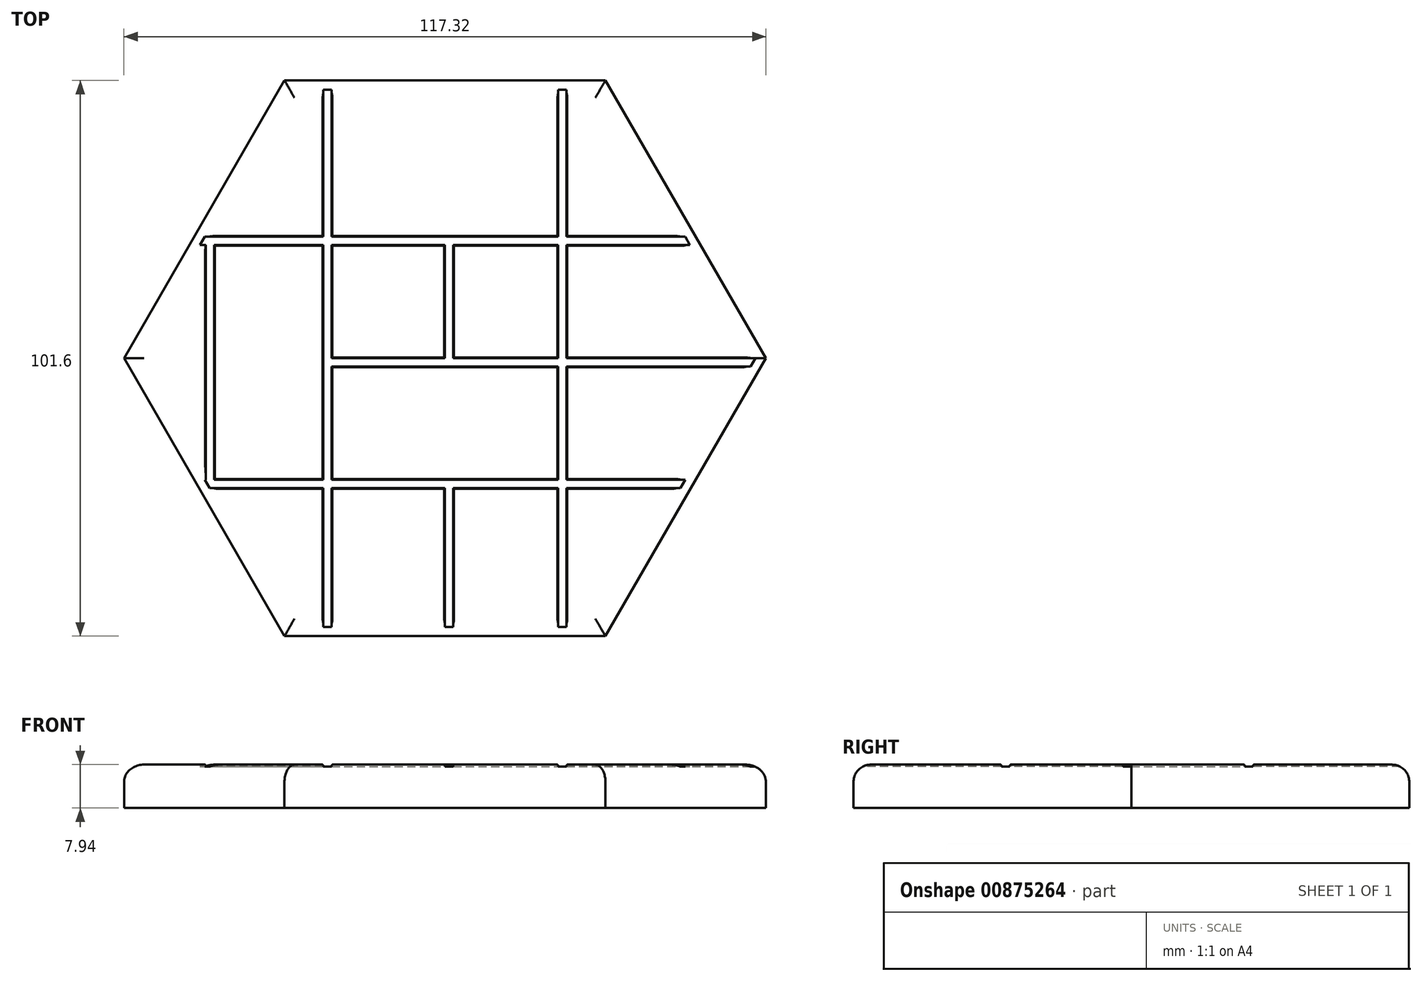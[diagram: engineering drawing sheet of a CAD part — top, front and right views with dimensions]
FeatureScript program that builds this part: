
annotation { "Feature Type Name" : "Feature", "Feature Type Description" : "" }
export const myFeature = defineFeature(function(context is Context, id is Id, definition is map)
    precondition{}
    {
        {
            var Q0;
            Q0=qCreatedBy(makeId("Top.planeOp"),FACE);
            var sketch = newSketch(context, id + "F0", { "sketchPlane" : qUnion([Q0])});
            skCircle(sketch, "E0.cCircle", {"center": v(0, 0) * mm, "radius": 50.8 * mm, "construction": true});
            skLineSegment(sketch, "E0.0", {"start": v(58.66, 0) * mm, "end": v(29.33, -50.8) * mm});
            skLineSegment(sketch, "E0.1", {"start": v(29.33, -50.8) * mm, "end": v(-29.33, -50.8) * mm});
            skLineSegment(sketch, "E0.2", {"start": v(-29.33, -50.8) * mm, "end": v(-58.66, 0) * mm});
            skLineSegment(sketch, "E0.3", {"start": v(-58.66, 0) * mm, "end": v(-29.33, 50.8) * mm});
            skLineSegment(sketch, "E0.4", {"start": v(-29.33, 50.8) * mm, "end": v(29.33, 50.8) * mm});
            skLineSegment(sketch, "E0.5", {"start": v(29.33, 50.8) * mm, "end": v(58.66, 0) * mm});
            skPoint(sketch, "E0.0.midPoint", {"position": v(44, -25.4) * mm});
            skSolve(sketch);
        }
        {
            var Q0;
            Q0 = qSketchRegion(id + "F0", true);
            extrude(context, id + "F1", {"entities" : qUnion([Q0]), "depth" : 7.94 * mm, "offsetDistance" : 25.4 * mm});
        }
        {
            var Q0;
            Q0=makeQuery(id+"F1.opExtrude","CAP_EDGE",EDGE,{"disambiguationData":[OSD([sQuery(id+"F0.wireOp",EDGE,"E0.2")])],"isStart":false});
            var Q1;
            Q1=makeQuery(id+"F1.opExtrude","CAP_EDGE",EDGE,{"disambiguationData":[OSD([sQuery(id+"F0.wireOp",EDGE,"E0.1")])],"isStart":false});
            var Q2;
            Q2=makeQuery(id+"F1.opExtrude","CAP_EDGE",EDGE,{"disambiguationData":[OSD([sQuery(id+"F0.wireOp",EDGE,"E0.0")])],"isStart":false});
            var Q3;
            Q3=makeQuery(id+"F1.opExtrude","CAP_EDGE",EDGE,{"disambiguationData":[OSD([sQuery(id+"F0.wireOp",EDGE,"E0.5")])],"isStart":false});
            var Q4;
            Q4=makeQuery(id+"F1.opExtrude","CAP_EDGE",EDGE,{"disambiguationData":[OSD([sQuery(id+"F0.wireOp",EDGE,"E0.4")])],"isStart":false});
            var Q5;
            Q5=makeQuery(id+"F1.opExtrude","CAP_EDGE",EDGE,{"disambiguationData":[OSD([sQuery(id+"F0.wireOp",EDGE,"E0.3")])],"isStart":false});
            fillet(context, id + "F2", {"entities" : qUnion([Q0, Q1, Q2, Q3, Q4, Q5]), "radius" : 3.17 * mm, "tangentPropagation" : true, "allowEdgeOverflow" : false});
        }
        {
            var Q0;
            Q0=makeQuery(id+"F1.opExtrude","CAP_FACE",FACE,{"disambiguationData":[OSD([sQuery(id+"F0.wireOp",EDGE,"E0.0"),sQuery(id+"F0.wireOp",EDGE,"E0.1"),sQuery(id+"F0.wireOp",EDGE,"E0.2"),sQuery(id+"F0.wireOp",EDGE,"E0.3"),sQuery(id+"F0.wireOp",EDGE,"E0.4"),sQuery(id+"F0.wireOp",EDGE,"E0.5")])],"isStart":false});
            var sketch = newSketch(context, id + "F3", { "sketchPlane" : qUnion([Q0])});
            skLineSegment(sketch, "E1", {"start": v(-22.23, 58.85) * mm, "end": v(-22.22, -59.57) * mm});
            skLineSegment(sketch, "E2", {"start": v(22.22, 59.72) * mm, "end": v(22.23, -61.08) * mm});
            skLineSegment(sketch, "E3", {"start": v(-65.38, 22.23) * mm, "end": v(65.6, 22.23) * mm});
            skLineSegment(sketch, "E4", {"start": v(-66.46, -22.23) * mm, "end": v(67.33, -22.23) * mm});
            skLineSegment(sketch, "E5", {"start": v(-22.23, 0) * mm, "end": v(71.88, 0) * mm});
            skPoint(sketch, "E5.startSnap0", {"position": v(-22.23, -0.36) * mm});
            skLineSegment(sketch, "E6", {"start": v(-42.16, -22.23) * mm, "end": v(-42.16, 22.23) * mm});
            skLineSegment(sketch, "E7", {"start": v(0, -57.56) * mm, "end": v(0, -22.23) * mm});
            skLineSegment(sketch, "E8", {"start": v(0, 0) * mm, "end": v(0, 22.23) * mm});
            skLineSegment(sketch, "E9.0", {"start": v(-20.7, 58.85) * mm, "end": v(-20.7, -59.57) * mm});
            skLineSegment(sketch, "E10.0", {"start": v(20.7, 59.72) * mm, "end": v(20.7, -61.08) * mm});
            skLineSegment(sketch, "E11.0", {"start": v(-65.38, 20.7) * mm, "end": v(65.6, 20.7) * mm});
            skLineSegment(sketch, "E12.0", {"start": v(1.52, 0) * mm, "end": v(1.52, 22.23) * mm});
            skLineSegment(sketch, "E13.0", {"start": v(-66.46, -23.75) * mm, "end": v(67.33, -23.75) * mm});
            skLineSegment(sketch, "E14.0", {"start": v(-22.23, -1.52) * mm, "end": v(71.88, -1.52) * mm});
            skLineSegment(sketch, "E15.0", {"start": v(-43.69, -22.23) * mm, "end": v(-43.69, 22.23) * mm});
            skLineSegment(sketch, "E16.0", {"start": v(1.52, -57.64) * mm, "end": v(1.52, -22.23) * mm});
            skLineSegment(sketch, "E17", {"start": v(-65.38, 22.23) * mm, "end": v(-65.38, 20.7) * mm});
            skLineSegment(sketch, "E18", {"start": v(-66.46, -22.23) * mm, "end": v(-66.46, -23.75) * mm});
            skLineSegment(sketch, "E19", {"start": v(-22.23, 58.85) * mm, "end": v(-20.7, 58.85) * mm});
            skLineSegment(sketch, "E20", {"start": v(22.22, 59.72) * mm, "end": v(20.7, 59.72) * mm});
            skLineSegment(sketch, "E21", {"start": v(65.6, 20.7) * mm, "end": v(65.6, 22.23) * mm});
            skLineSegment(sketch, "E22", {"start": v(71.88, 0) * mm, "end": v(71.88, -1.52) * mm});
            skLineSegment(sketch, "E23", {"start": v(67.33, -22.23) * mm, "end": v(67.33, -23.75) * mm});
            skLineSegment(sketch, "E24", {"start": v(22.23, -61.08) * mm, "end": v(20.7, -61.08) * mm});
            skLineSegment(sketch, "E25", {"start": v(1.52, -57.64) * mm, "end": v(0, -57.56) * mm});
            skLineSegment(sketch, "E26", {"start": v(-20.7, -59.57) * mm, "end": v(-22.22, -59.57) * mm});
            skSolve(sketch);
        }
        {
            var Q0;
            {var subQ0=sQuery(id+"F3.wireOp",EDGE,"E19");Q0=makeQuery(id+"F3.imprint","IMPRINT",FACE,{"disambiguationData":[TD([[makeQuery(id+"F3.imprint","IMPRINT",EDGE,{"derivedFrom":subQ0}),-1.0]])]});}
            var Q1;
            {var subQ0=sQuery(id+"F3.wireOp",EDGE,"E3");var subQ1=sQuery(id+"F3.wireOp",EDGE,"E1");var subQ2=makeQuery(id+"F3.imprint","INTERSECT",VERTEX,{"derivedFrom":[subQ1,subQ0]});Q1=makeQuery(id+"F3.imprint","IMPRINT",FACE,{"disambiguationData":[TD([[makeQuery(id+"F3.imprint","IMPRINT",EDGE,{"disambiguationData":[TD([[subQ2,-1.0]])],"derivedFrom":subQ0}),1.0]])]});}
            var Q2;
            {var subQ0=sQuery(id+"F3.wireOp",EDGE,"E3");var subQ1=sQuery(id+"F3.wireOp",EDGE,"E2");var subQ2=makeQuery(id+"F3.imprint","INTERSECT",VERTEX,{"derivedFrom":[subQ1,subQ0]});Q2=makeQuery(id+"F3.imprint","IMPRINT",FACE,{"disambiguationData":[TD([[makeQuery(id+"F3.imprint","IMPRINT",EDGE,{"disambiguationData":[TD([[subQ2,1.0]])],"derivedFrom":subQ0}),1.0]])]});}
            var Q3;
            {var subQ0=sQuery(id+"F3.wireOp",EDGE,"E20");Q3=makeQuery(id+"F3.imprint","IMPRINT",FACE,{"disambiguationData":[TD([[makeQuery(id+"F3.imprint","IMPRINT",EDGE,{"derivedFrom":subQ0}),1.0]])]});}
            var Q4;
            {var subQ0=sQuery(id+"F3.wireOp",EDGE,"E3");var subQ1=sQuery(id+"F3.wireOp",EDGE,"E2");var subQ2=makeQuery(id+"F3.imprint","INTERSECT",VERTEX,{"derivedFrom":[subQ1,subQ0]});Q4=makeQuery(id+"F3.imprint","IMPRINT",FACE,{"disambiguationData":[TD([[makeQuery(id+"F3.imprint","IMPRINT",EDGE,{"disambiguationData":[TD([[subQ2,-1.0]])],"derivedFrom":subQ1}),1.0]])]});}
            var Q5;
            {var subQ0=sQuery(id+"F3.wireOp",EDGE,"E21");Q5=makeQuery(id+"F3.imprint","IMPRINT",FACE,{"disambiguationData":[TD([[makeQuery(id+"F3.imprint","IMPRINT",EDGE,{"derivedFrom":subQ0}),1.0]])]});}
            var Q6;
            {var subQ0=sQuery(id+"F3.wireOp",EDGE,"E3");var subQ1=sQuery(id+"F3.wireOp",EDGE,"E2");var subQ2=makeQuery(id+"F3.imprint","INTERSECT",VERTEX,{"derivedFrom":[subQ1,subQ0]});Q6=makeQuery(id+"F3.imprint","IMPRINT",FACE,{"disambiguationData":[TD([[makeQuery(id+"F3.imprint","IMPRINT",EDGE,{"disambiguationData":[TD([[subQ2,-1.0]])],"derivedFrom":subQ1}),-1.0]])]});}
            var Q7;
            {var subQ0=sQuery(id+"F3.wireOp",EDGE,"E11.0");var subQ1=sQuery(id+"F3.wireOp",EDGE,"E2");var subQ2=makeQuery(id+"F3.imprint","INTERSECT",VERTEX,{"derivedFrom":[subQ1,subQ0]});Q7=makeQuery(id+"F3.imprint","IMPRINT",FACE,{"disambiguationData":[TD([[makeQuery(id+"F3.imprint","IMPRINT",EDGE,{"disambiguationData":[TD([[subQ2,-1.0]])],"derivedFrom":subQ1}),-1.0]])]});}
            var Q8;
            {var subQ0=sQuery(id+"F3.wireOp",EDGE,"E12.0");var subQ1=sQuery(id+"F3.wireOp",EDGE,"E3");var subQ2=makeQuery(id+"F3.imprint","INTERSECT",VERTEX,{"derivedFrom":[subQ1,subQ0]});Q8=makeQuery(id+"F3.imprint","IMPRINT",FACE,{"disambiguationData":[TD([[makeQuery(id+"F3.imprint","IMPRINT",EDGE,{"disambiguationData":[TD([[subQ2,-1.0]])],"derivedFrom":subQ1}),-1.0]])]});}
            var Q9;
            {var subQ0=sQuery(id+"F3.wireOp",EDGE,"E5");var subQ1=sQuery(id+"F3.wireOp",EDGE,"E2");var subQ2=makeQuery(id+"F3.imprint","INTERSECT",VERTEX,{"derivedFrom":[subQ1,subQ0]});Q9=makeQuery(id+"F3.imprint","IMPRINT",FACE,{"disambiguationData":[TD([[makeQuery(id+"F3.imprint","IMPRINT",EDGE,{"disambiguationData":[TD([[subQ2,-1.0]])],"derivedFrom":subQ1}),1.0]])]});}
            var Q10;
            {var subQ0=sQuery(id+"F3.wireOp",EDGE,"E5");var subQ1=sQuery(id+"F3.wireOp",EDGE,"E2");var subQ2=makeQuery(id+"F3.imprint","INTERSECT",VERTEX,{"derivedFrom":[subQ1,subQ0]});Q10=makeQuery(id+"F3.imprint","IMPRINT",FACE,{"disambiguationData":[TD([[makeQuery(id+"F3.imprint","IMPRINT",EDGE,{"disambiguationData":[TD([[subQ2,-1.0]])],"derivedFrom":subQ1}),-1.0]])]});}
            var Q11;
            {var subQ1=sQuery(id+"F3.wireOp",EDGE,"E5");var subQ8=makeQuery(id+"F3.imprint","INTERSECT",VERTEX,{"derivedFrom":[subQ1,sQuery(id+"F3.wireOp",EDGE,"E8")]});Q11=makeQuery(id+"F3.imprint","IMPRINT",FACE,{"disambiguationData":[TD([[makeQuery(id+"F3.imprint","IMPRINT",EDGE,{"disambiguationData":[TD([[subQ8,1.0]])],"derivedFrom":subQ1}),-1.0]])]});}
            var Q12;
            {var subQ0=sQuery(id+"F3.wireOp",EDGE,"E14.0");var subQ1=sQuery(id+"F3.wireOp",EDGE,"E2");var subQ2=makeQuery(id+"F3.imprint","INTERSECT",VERTEX,{"derivedFrom":[subQ1,subQ0]});Q12=makeQuery(id+"F3.imprint","IMPRINT",FACE,{"disambiguationData":[TD([[makeQuery(id+"F3.imprint","IMPRINT",EDGE,{"disambiguationData":[TD([[subQ2,-1.0]])],"derivedFrom":subQ1}),-1.0]])]});}
            var Q13;
            {var subQ0=sQuery(id+"F3.wireOp",EDGE,"E8");var subQ1=sQuery(id+"F3.wireOp",EDGE,"E5");var subQ2=makeQuery(id+"F3.imprint","INTERSECT",VERTEX,{"derivedFrom":[subQ1,subQ0]});Q13=makeQuery(id+"F3.imprint","IMPRINT",FACE,{"disambiguationData":[TD([[makeQuery(id+"F3.imprint","IMPRINT",EDGE,{"disambiguationData":[TD([[subQ2,-1.0]])],"derivedFrom":subQ1}),1.0]])]});}
            var Q14;
            {var subQ0=sQuery(id+"F3.wireOp",EDGE,"E8");var subQ1=sQuery(id+"F3.wireOp",EDGE,"E3");var subQ2=makeQuery(id+"F3.imprint","INTERSECT",VERTEX,{"derivedFrom":[subQ1,subQ0]});Q14=makeQuery(id+"F3.imprint","IMPRINT",FACE,{"disambiguationData":[TD([[makeQuery(id+"F3.imprint","IMPRINT",EDGE,{"disambiguationData":[TD([[subQ2,-1.0]])],"derivedFrom":subQ1}),-1.0]])]});}
            var Q15;
            {var subQ0=sQuery(id+"F3.wireOp",EDGE,"E8");var subQ1=sQuery(id+"F3.wireOp",EDGE,"E3");var subQ2=makeQuery(id+"F3.imprint","INTERSECT",VERTEX,{"derivedFrom":[subQ1,subQ0]});Q15=makeQuery(id+"F3.imprint","IMPRINT",FACE,{"disambiguationData":[TD([[makeQuery(id+"F3.imprint","IMPRINT",EDGE,{"disambiguationData":[TD([[subQ2,1.0]])],"derivedFrom":subQ1}),-1.0]])]});}
            var Q16;
            {var subQ0=sQuery(id+"F3.wireOp",EDGE,"E3");var subQ1=sQuery(id+"F3.wireOp",EDGE,"E1");var subQ2=makeQuery(id+"F3.imprint","INTERSECT",VERTEX,{"derivedFrom":[subQ1,subQ0]});Q16=makeQuery(id+"F3.imprint","IMPRINT",FACE,{"disambiguationData":[TD([[makeQuery(id+"F3.imprint","IMPRINT",EDGE,{"disambiguationData":[TD([[subQ2,-1.0]])],"derivedFrom":subQ1}),1.0]])]});}
            var Q17;
            {var subQ0=sQuery(id+"F3.wireOp",EDGE,"E5");var subQ1=sQuery(id+"F3.wireOp",EDGE,"E1");var subQ2=makeQuery(id+"F3.imprint","INTERSECT",VERTEX,{"derivedFrom":[subQ1,subQ0]});Q17=makeQuery(id+"F3.imprint","IMPRINT",FACE,{"disambiguationData":[TD([[makeQuery(id+"F3.imprint","IMPRINT",EDGE,{"disambiguationData":[TD([[subQ2,1.0]])],"derivedFrom":subQ1}),1.0]])]});}
            var Q18;
            {var subQ0=sQuery(id+"F3.wireOp",EDGE,"E3");var subQ1=sQuery(id+"F3.wireOp",EDGE,"E1");var subQ2=makeQuery(id+"F3.imprint","INTERSECT",VERTEX,{"derivedFrom":[subQ1,subQ0]});Q18=makeQuery(id+"F3.imprint","IMPRINT",FACE,{"disambiguationData":[TD([[makeQuery(id+"F3.imprint","IMPRINT",EDGE,{"disambiguationData":[TD([[subQ2,-1.0]])],"derivedFrom":subQ1}),-1.0]])]});}
            var Q19;
            {var subQ8=sQuery(id+"F3.wireOp",EDGE,"E11.0");var subQ9=sQuery(id+"F3.wireOp",EDGE,"E6");var subQ10=makeQuery(id+"F3.imprint","INTERSECT",VERTEX,{"derivedFrom":[subQ9,subQ8]});Q19=makeQuery(id+"F3.imprint","IMPRINT",FACE,{"disambiguationData":[TD([[makeQuery(id+"F3.imprint","IMPRINT",EDGE,{"disambiguationData":[TD([[subQ10,1.0]])],"derivedFrom":subQ8}),-1.0]])]});}
            var Q20;
            {var subQ0=sQuery(id+"F3.wireOp",EDGE,"E17");Q20=makeQuery(id+"F3.imprint","IMPRINT",FACE,{"disambiguationData":[TD([[makeQuery(id+"F3.imprint","IMPRINT",EDGE,{"derivedFrom":subQ0}),1.0]])]});}
            var Q21;
            {var subQ0=sQuery(id+"F3.wireOp",EDGE,"E6");var subQ4=sQuery(id+"F3.wireOp",EDGE,"E11.0");var subQ5=makeQuery(id+"F3.imprint","INTERSECT",VERTEX,{"derivedFrom":[subQ0,subQ4]});Q21=makeQuery(id+"F3.imprint","IMPRINT",FACE,{"disambiguationData":[TD([[makeQuery(id+"F3.imprint","IMPRINT",EDGE,{"disambiguationData":[TD([[subQ5,1.0]])],"derivedFrom":subQ4}),1.0]])]});}
            var Q22;
            {var subQ0=sQuery(id+"F3.wireOp",EDGE,"E3");var subQ4=sQuery(id+"F3.wireOp",EDGE,"E15.0");var subQ5=makeQuery(id+"F3.imprint","INTERSECT",VERTEX,{"derivedFrom":[subQ0,subQ4]});Q22=makeQuery(id+"F3.imprint","IMPRINT",FACE,{"disambiguationData":[TD([[makeQuery(id+"F3.imprint","IMPRINT",EDGE,{"disambiguationData":[TD([[subQ5,1.0]])],"derivedFrom":subQ4}),-1.0]])]});}
            var Q23;
            {var subQ0=sQuery(id+"F3.wireOp",EDGE,"E15.0");var subQ1=sQuery(id+"F3.wireOp",EDGE,"E11.0");var subQ2=makeQuery(id+"F3.imprint","INTERSECT",VERTEX,{"derivedFrom":[subQ1,subQ0]});Q23=makeQuery(id+"F3.imprint","IMPRINT",FACE,{"disambiguationData":[TD([[makeQuery(id+"F3.imprint","IMPRINT",EDGE,{"disambiguationData":[TD([[subQ2,-1.0]])],"derivedFrom":subQ1}),-1.0]])]});}
            var Q24;
            {var subQ0=sQuery(id+"F3.wireOp",EDGE,"E18");Q24=makeQuery(id+"F3.imprint","IMPRINT",FACE,{"disambiguationData":[TD([[makeQuery(id+"F3.imprint","IMPRINT",EDGE,{"derivedFrom":subQ0}),1.0]])]});}
            var Q25;
            {var subQ0=sQuery(id+"F3.wireOp",EDGE,"E4");var subQ4=sQuery(id+"F3.wireOp",EDGE,"E15.0");var subQ5=makeQuery(id+"F3.imprint","INTERSECT",VERTEX,{"derivedFrom":[subQ0,subQ4]});Q25=makeQuery(id+"F3.imprint","IMPRINT",FACE,{"disambiguationData":[TD([[makeQuery(id+"F3.imprint","IMPRINT",EDGE,{"disambiguationData":[TD([[subQ5,-1.0]])],"derivedFrom":subQ4}),-1.0]])]});}
            var Q26;
            {var subQ0=sQuery(id+"F3.wireOp",EDGE,"E4");var subQ1=sQuery(id+"F3.wireOp",EDGE,"E1");var subQ2=makeQuery(id+"F3.imprint","INTERSECT",VERTEX,{"derivedFrom":[subQ1,subQ0]});Q26=makeQuery(id+"F3.imprint","IMPRINT",FACE,{"disambiguationData":[TD([[makeQuery(id+"F3.imprint","IMPRINT",EDGE,{"disambiguationData":[TD([[subQ2,-1.0]])],"derivedFrom":subQ1}),1.0]])]});}
            var Q27;
            {var subQ0=sQuery(id+"F3.wireOp",EDGE,"E14.0");var subQ1=sQuery(id+"F3.wireOp",EDGE,"E1");var subQ2=makeQuery(id+"F3.imprint","INTERSECT",VERTEX,{"derivedFrom":[subQ1,subQ0]});Q27=makeQuery(id+"F3.imprint","IMPRINT",FACE,{"disambiguationData":[TD([[makeQuery(id+"F3.imprint","IMPRINT",EDGE,{"disambiguationData":[TD([[subQ2,-1.0]])],"derivedFrom":subQ1}),1.0]])]});}
            var Q28;
            {var subQ0=sQuery(id+"F3.wireOp",EDGE,"E5");var subQ1=sQuery(id+"F3.wireOp",EDGE,"E1");var subQ2=makeQuery(id+"F3.imprint","INTERSECT",VERTEX,{"derivedFrom":[subQ1,subQ0]});Q28=makeQuery(id+"F3.imprint","IMPRINT",FACE,{"disambiguationData":[TD([[makeQuery(id+"F3.imprint","IMPRINT",EDGE,{"disambiguationData":[TD([[subQ2,-1.0]])],"derivedFrom":subQ1}),1.0]])]});}
            var Q29;
            {var subQ0=sQuery(id+"F3.wireOp",EDGE,"E13.0");var subQ1=sQuery(id+"F3.wireOp",EDGE,"E1");var subQ2=makeQuery(id+"F3.imprint","INTERSECT",VERTEX,{"derivedFrom":[subQ1,subQ0]});Q29=makeQuery(id+"F3.imprint","IMPRINT",FACE,{"disambiguationData":[TD([[makeQuery(id+"F3.imprint","IMPRINT",EDGE,{"disambiguationData":[TD([[subQ2,-1.0]])],"derivedFrom":subQ0}),-1.0]])]});}
            var Q30;
            {var subQ0=sQuery(id+"F3.wireOp",EDGE,"E7");var subQ1=sQuery(id+"F3.wireOp",EDGE,"E4");var subQ2=makeQuery(id+"F3.imprint","INTERSECT",VERTEX,{"derivedFrom":[subQ1,subQ0]});Q30=makeQuery(id+"F3.imprint","IMPRINT",FACE,{"disambiguationData":[TD([[makeQuery(id+"F3.imprint","IMPRINT",EDGE,{"disambiguationData":[TD([[subQ2,1.0]])],"derivedFrom":subQ1}),-1.0]])]});}
            var Q31;
            {var subQ0=sQuery(id+"F3.wireOp",EDGE,"E7");var subQ1=sQuery(id+"F3.wireOp",EDGE,"E4");var subQ2=makeQuery(id+"F3.imprint","INTERSECT",VERTEX,{"derivedFrom":[subQ1,subQ0]});Q31=makeQuery(id+"F3.imprint","IMPRINT",FACE,{"disambiguationData":[TD([[makeQuery(id+"F3.imprint","IMPRINT",EDGE,{"disambiguationData":[TD([[subQ2,-1.0]])],"derivedFrom":subQ1}),-1.0]])]});}
            var Q32;
            {var subQ0=sQuery(id+"F3.wireOp",EDGE,"E16.0");var subQ1=sQuery(id+"F3.wireOp",EDGE,"E4");var subQ2=makeQuery(id+"F3.imprint","INTERSECT",VERTEX,{"derivedFrom":[subQ1,subQ0]});Q32=makeQuery(id+"F3.imprint","IMPRINT",FACE,{"disambiguationData":[TD([[makeQuery(id+"F3.imprint","IMPRINT",EDGE,{"disambiguationData":[TD([[subQ2,-1.0]])],"derivedFrom":subQ1}),-1.0]])]});}
            var Q33;
            {var subQ0=sQuery(id+"F3.wireOp",EDGE,"E13.0");var subQ1=sQuery(id+"F3.wireOp",EDGE,"E7");var subQ2=makeQuery(id+"F3.imprint","INTERSECT",VERTEX,{"derivedFrom":[subQ1,subQ0]});Q33=makeQuery(id+"F3.imprint","IMPRINT",FACE,{"disambiguationData":[TD([[makeQuery(id+"F3.imprint","IMPRINT",EDGE,{"disambiguationData":[TD([[subQ2,-1.0]])],"derivedFrom":subQ0}),-1.0]])]});}
            var Q34;
            {var subQ6=sQuery(id+"F3.wireOp",EDGE,"E22");Q34=makeQuery(id+"F3.imprint","IMPRINT",FACE,{"disambiguationData":[TD([[makeQuery(id+"F3.imprint","IMPRINT",EDGE,{"derivedFrom":subQ6}),-1.0]])]});}
            var Q35;
            {var subQ0=sQuery(id+"F3.wireOp",EDGE,"E23");Q35=makeQuery(id+"F3.imprint","IMPRINT",FACE,{"disambiguationData":[TD([[makeQuery(id+"F3.imprint","IMPRINT",EDGE,{"derivedFrom":subQ0}),-1.0]])]});}
            var Q36;
            {var subQ0=sQuery(id+"F3.wireOp",EDGE,"E4");var subQ1=sQuery(id+"F3.wireOp",EDGE,"E2");var subQ2=makeQuery(id+"F3.imprint","INTERSECT",VERTEX,{"derivedFrom":[subQ1,subQ0]});Q36=makeQuery(id+"F3.imprint","IMPRINT",FACE,{"disambiguationData":[TD([[makeQuery(id+"F3.imprint","IMPRINT",EDGE,{"disambiguationData":[TD([[subQ2,-1.0]])],"derivedFrom":subQ1}),1.0]])]});}
            var Q37;
            {var subQ0=sQuery(id+"F3.wireOp",EDGE,"E4");var subQ1=sQuery(id+"F3.wireOp",EDGE,"E2");var subQ2=makeQuery(id+"F3.imprint","INTERSECT",VERTEX,{"derivedFrom":[subQ1,subQ0]});Q37=makeQuery(id+"F3.imprint","IMPRINT",FACE,{"disambiguationData":[TD([[makeQuery(id+"F3.imprint","IMPRINT",EDGE,{"disambiguationData":[TD([[subQ2,-1.0]])],"derivedFrom":subQ1}),-1.0]])]});}
            var Q38;
            {var subQ0=sQuery(id+"F3.wireOp",EDGE,"E24");Q38=makeQuery(id+"F3.imprint","IMPRINT",FACE,{"disambiguationData":[TD([[makeQuery(id+"F3.imprint","IMPRINT",EDGE,{"derivedFrom":subQ0}),-1.0]])]});}
            var Q39;
            {var subQ0=sQuery(id+"F3.wireOp",EDGE,"E13.0");var subQ1=sQuery(id+"F3.wireOp",EDGE,"E2");var subQ2=makeQuery(id+"F3.imprint","INTERSECT",VERTEX,{"derivedFrom":[subQ1,subQ0]});Q39=makeQuery(id+"F3.imprint","IMPRINT",FACE,{"disambiguationData":[TD([[makeQuery(id+"F3.imprint","IMPRINT",EDGE,{"disambiguationData":[TD([[subQ2,1.0]])],"derivedFrom":subQ0}),-1.0]])]});}
            var Q40;
            {var subQ0=sQuery(id+"F3.wireOp",EDGE,"E25");Q40=makeQuery(id+"F3.imprint","IMPRINT",FACE,{"disambiguationData":[TD([[makeQuery(id+"F3.imprint","IMPRINT",EDGE,{"derivedFrom":subQ0}),-1.0]])]});}
            var Q41;
            {var subQ0=sQuery(id+"F3.wireOp",EDGE,"E26");Q41=makeQuery(id+"F3.imprint","IMPRINT",FACE,{"disambiguationData":[TD([[makeQuery(id+"F3.imprint","IMPRINT",EDGE,{"derivedFrom":subQ0}),-1.0]])]});}
            var Q42;
            {var subQ0=sQuery(id+"F3.wireOp",EDGE,"E4");var subQ1=sQuery(id+"F3.wireOp",EDGE,"E1");var subQ2=makeQuery(id+"F3.imprint","INTERSECT",VERTEX,{"derivedFrom":[subQ1,subQ0]});Q42=makeQuery(id+"F3.imprint","IMPRINT",FACE,{"disambiguationData":[TD([[makeQuery(id+"F3.imprint","IMPRINT",EDGE,{"disambiguationData":[TD([[subQ2,-1.0]])],"derivedFrom":subQ1}),-1.0]])]});}
            extrude(context, id + "F4", {"entities" : qUnion([Q0, Q1, Q2, Q3, Q4, Q5, Q6, Q7, Q8, Q9, Q10, Q11, Q12, Q13, Q14, Q15, Q16, Q17, Q18, Q19, Q20, Q21, Q22, Q23, Q24, Q25, Q26, Q27, Q28, Q29, Q30, Q31, Q32, Q33, Q34, Q35, Q36, Q37, Q38, Q39, Q40, Q41, Q42]), "operationType" : NewBodyOperationType.REMOVE, "oppositeDirection" : true, "depth" : 0.38 * mm, "offsetDistance" : 25.4 * mm});
        }
        {
            var Q0;
            {var subQ0=sQuery(id+"F0.wireOp",EDGE,"E0.1");var subQ1=sQuery(id+"F3.wireOp",EDGE,"E7");var subQ3=makeQuery(id+"F1.opExtrude","CAP_FACE",FACE,{"disambiguationData":[OSD([sQuery(id+"F0.wireOp",EDGE,"E0.0"),subQ0,sQuery(id+"F0.wireOp",EDGE,"E0.2"),sQuery(id+"F0.wireOp",EDGE,"E0.3"),sQuery(id+"F0.wireOp",EDGE,"E0.4"),sQuery(id+"F0.wireOp",EDGE,"E0.5")])],"isStart":false});Q0=makeQuery(id+"F4.boolean.opBoolean","SPLIT",FACE,{"disambiguationData":[TD([makeQuery(id+"F4.opExtrude","SWEPT_FACE",FACE,{"disambiguationData":[OSD([subQ1])]})])],"derivedFrom":subQ3});}
            var Q1;
            {var subQ0=sQuery(id+"F3.wireOp",EDGE,"E4");var subQ5=sQuery(id+"F3.wireOp",EDGE,"E9.0");var subQ6=makeQuery(id+"F3.imprint","INTERSECT",VERTEX,{"derivedFrom":[subQ0,subQ5]});Q1=makeQuery(id+"F4.boolean.opBoolean","SPLIT",FACE,{"disambiguationData":[TD([makeQuery(id+"F4.opExtrude","SWEPT_FACE",FACE,{"disambiguationData":[OSD([subQ5]),TDD([makeQuery(id+"F3.imprint","IMPRINT",EDGE,{"disambiguationData":[TD([[subQ6,1.0]])],"derivedFrom":subQ5})])]})])],"derivedFrom":makeQuery(id+"F1.opExtrude","CAP_FACE",FACE,{"disambiguationData":[OSD([sQuery(id+"F0.wireOp",EDGE,"E0.0"),sQuery(id+"F0.wireOp",EDGE,"E0.1"),sQuery(id+"F0.wireOp",EDGE,"E0.2"),sQuery(id+"F0.wireOp",EDGE,"E0.3"),sQuery(id+"F0.wireOp",EDGE,"E0.4"),sQuery(id+"F0.wireOp",EDGE,"E0.5")])],"isStart":false})});}
            var Q2;
            {var subQ0=sQuery(id+"F0.wireOp",EDGE,"E0.1");var subQ4=sQuery(id+"F3.wireOp",EDGE,"E16.0");var subQ5=makeQuery(id+"F1.opExtrude","CAP_FACE",FACE,{"disambiguationData":[OSD([sQuery(id+"F0.wireOp",EDGE,"E0.0"),subQ0,sQuery(id+"F0.wireOp",EDGE,"E0.2"),sQuery(id+"F0.wireOp",EDGE,"E0.3"),sQuery(id+"F0.wireOp",EDGE,"E0.4"),sQuery(id+"F0.wireOp",EDGE,"E0.5")])],"isStart":false});Q2=makeQuery(id+"F4.boolean.opBoolean","SPLIT",FACE,{"disambiguationData":[TD([makeQuery(id+"F4.opExtrude","SWEPT_FACE",FACE,{"disambiguationData":[OSD([subQ4])]})])],"derivedFrom":subQ5});}
            var Q3;
            {var subQ0=sQuery(id+"F0.wireOp",EDGE,"E0.0");var subQ1=sQuery(id+"F0.wireOp",EDGE,"E0.1");var subQ2=sQuery(id+"F3.wireOp",EDGE,"E2");var subQ3=makeQuery(id+"F1.opExtrude","CAP_FACE",FACE,{"disambiguationData":[OSD([subQ0,subQ1,sQuery(id+"F0.wireOp",EDGE,"E0.2"),sQuery(id+"F0.wireOp",EDGE,"E0.3"),sQuery(id+"F0.wireOp",EDGE,"E0.4"),sQuery(id+"F0.wireOp",EDGE,"E0.5")])],"isStart":false});var subQ5=sQuery(id+"F3.wireOp",EDGE,"E13.0");var subQ6=makeQuery(id+"F3.imprint","INTERSECT",VERTEX,{"derivedFrom":[subQ2,subQ5]});Q3=makeQuery(id+"F4.boolean.opBoolean","SPLIT",FACE,{"disambiguationData":[TD([makeQuery(id+"F4.opExtrude","SWEPT_FACE",FACE,{"disambiguationData":[OSD([subQ2]),TDD([makeQuery(id+"F3.imprint","IMPRINT",EDGE,{"disambiguationData":[TD([[subQ6,-1.0]])],"derivedFrom":subQ2}),makeQuery(id+"F3.imprint","IMPRINT",EDGE,{"disambiguationData":[TD([[makeQuery(id+"F3.imprint","INTERSECT",VERTEX,{"derivedFrom":[subQ2,sQuery(id+"F3.wireOp",EDGE,"E24")]}),1.0]])],"derivedFrom":subQ2})])]})])],"derivedFrom":subQ3});}
            var Q4;
            {var subQ0=sQuery(id+"F0.wireOp",EDGE,"E0.1");var subQ1=sQuery(id+"F0.wireOp",EDGE,"E0.2");var subQ2=sQuery(id+"F3.wireOp",EDGE,"E1");var subQ3=makeQuery(id+"F1.opExtrude","CAP_FACE",FACE,{"disambiguationData":[OSD([sQuery(id+"F0.wireOp",EDGE,"E0.0"),subQ0,subQ1,sQuery(id+"F0.wireOp",EDGE,"E0.3"),sQuery(id+"F0.wireOp",EDGE,"E0.4"),sQuery(id+"F0.wireOp",EDGE,"E0.5")])],"isStart":false});var subQ5=sQuery(id+"F3.wireOp",EDGE,"E13.0");var subQ6=makeQuery(id+"F3.imprint","INTERSECT",VERTEX,{"derivedFrom":[subQ2,subQ5]});Q4=makeQuery(id+"F4.boolean.opBoolean","SPLIT",FACE,{"disambiguationData":[TD([makeQuery(id+"F4.opExtrude","SWEPT_FACE",FACE,{"disambiguationData":[OSD([subQ2]),TDD([makeQuery(id+"F3.imprint","IMPRINT",EDGE,{"disambiguationData":[TD([[subQ6,-1.0]])],"derivedFrom":subQ2}),makeQuery(id+"F3.imprint","IMPRINT",EDGE,{"disambiguationData":[TD([[makeQuery(id+"F3.imprint","INTERSECT",VERTEX,{"derivedFrom":[subQ2,sQuery(id+"F3.wireOp",EDGE,"E26")]}),1.0]])],"derivedFrom":subQ2})])]})])],"derivedFrom":subQ3});}
            var Q5;
            {var subQ0=sQuery(id+"F0.wireOp",EDGE,"E0.2");var subQ1=sQuery(id+"F0.wireOp",EDGE,"E0.3");Q5=makeQuery(id+"F4.boolean.opBoolean","SPLIT",FACE,{"disambiguationData":[TD([makeQuery(id+"F4.opExtrude","SWEPT_FACE",FACE,{"disambiguationData":[OSD([sQuery(id+"F3.wireOp",EDGE,"E15.0")])]})])],"derivedFrom":makeQuery(id+"F1.opExtrude","CAP_FACE",FACE,{"disambiguationData":[OSD([sQuery(id+"F0.wireOp",EDGE,"E0.0"),sQuery(id+"F0.wireOp",EDGE,"E0.1"),subQ0,subQ1,sQuery(id+"F0.wireOp",EDGE,"E0.4"),sQuery(id+"F0.wireOp",EDGE,"E0.5")])],"isStart":false})});}
            var Q6;
            {var subQ0=sQuery(id+"F3.wireOp",EDGE,"E8");Q6=makeQuery(id+"F4.boolean.opBoolean","SPLIT",FACE,{"disambiguationData":[TD([makeQuery(id+"F4.opExtrude","SWEPT_FACE",FACE,{"disambiguationData":[OSD([subQ0])]})])],"derivedFrom":makeQuery(id+"F1.opExtrude","CAP_FACE",FACE,{"disambiguationData":[OSD([sQuery(id+"F0.wireOp",EDGE,"E0.0"),sQuery(id+"F0.wireOp",EDGE,"E0.1"),sQuery(id+"F0.wireOp",EDGE,"E0.2"),sQuery(id+"F0.wireOp",EDGE,"E0.3"),sQuery(id+"F0.wireOp",EDGE,"E0.4"),sQuery(id+"F0.wireOp",EDGE,"E0.5")])],"isStart":false})});}
            var Q7;
            {var subQ0=sQuery(id+"F3.wireOp",EDGE,"E12.0");Q7=makeQuery(id+"F4.boolean.opBoolean","SPLIT",FACE,{"disambiguationData":[TD([makeQuery(id+"F4.opExtrude","SWEPT_FACE",FACE,{"disambiguationData":[OSD([subQ0])]})])],"derivedFrom":makeQuery(id+"F1.opExtrude","CAP_FACE",FACE,{"disambiguationData":[OSD([sQuery(id+"F0.wireOp",EDGE,"E0.0"),sQuery(id+"F0.wireOp",EDGE,"E0.1"),sQuery(id+"F0.wireOp",EDGE,"E0.2"),sQuery(id+"F0.wireOp",EDGE,"E0.3"),sQuery(id+"F0.wireOp",EDGE,"E0.4"),sQuery(id+"F0.wireOp",EDGE,"E0.5")])],"isStart":false})});}
            var Q8;
            {var subQ0=sQuery(id+"F0.wireOp",EDGE,"E0.0");var subQ1=sQuery(id+"F3.wireOp",EDGE,"E14.0");var subQ2=sQuery(id+"F3.wireOp",EDGE,"E2");var subQ3=makeQuery(id+"F3.imprint","INTERSECT",VERTEX,{"derivedFrom":[subQ2,subQ1]});var subQ6=makeQuery(id+"F1.opExtrude","CAP_FACE",FACE,{"disambiguationData":[OSD([subQ0,sQuery(id+"F0.wireOp",EDGE,"E0.1"),sQuery(id+"F0.wireOp",EDGE,"E0.2"),sQuery(id+"F0.wireOp",EDGE,"E0.3"),sQuery(id+"F0.wireOp",EDGE,"E0.4"),sQuery(id+"F0.wireOp",EDGE,"E0.5")])],"isStart":false});Q8=makeQuery(id+"F4.boolean.opBoolean","SPLIT",FACE,{"disambiguationData":[TD([makeQuery(id+"F4.opExtrude","SWEPT_FACE",FACE,{"disambiguationData":[OSD([subQ2]),TDD([makeQuery(id+"F3.imprint","IMPRINT",EDGE,{"disambiguationData":[TD([[subQ3,-1.0]])],"derivedFrom":subQ2})])]})])],"derivedFrom":subQ6});}
            var Q9;
            {var subQ0=sQuery(id+"F0.wireOp",EDGE,"E0.4");var subQ1=sQuery(id+"F3.wireOp",EDGE,"E3");var subQ2=sQuery(id+"F0.wireOp",EDGE,"E0.5");var subQ3=makeQuery(id+"F1.opExtrude","CAP_FACE",FACE,{"disambiguationData":[OSD([sQuery(id+"F0.wireOp",EDGE,"E0.0"),sQuery(id+"F0.wireOp",EDGE,"E0.1"),sQuery(id+"F0.wireOp",EDGE,"E0.2"),sQuery(id+"F0.wireOp",EDGE,"E0.3"),subQ0,subQ2])],"isStart":false});var subQ5=sQuery(id+"F3.wireOp",EDGE,"E2");var subQ6=makeQuery(id+"F3.imprint","INTERSECT",VERTEX,{"derivedFrom":[subQ5,subQ1]});Q9=makeQuery(id+"F4.boolean.opBoolean","SPLIT",FACE,{"disambiguationData":[TD([makeQuery(id+"F4.opExtrude","SWEPT_FACE",FACE,{"disambiguationData":[OSD([subQ5]),TDD([makeQuery(id+"F3.imprint","IMPRINT",EDGE,{"disambiguationData":[TD([[makeQuery(id+"F3.imprint","INTERSECT",VERTEX,{"derivedFrom":[subQ5,sQuery(id+"F3.wireOp",EDGE,"E20")]}),-1.0]])],"derivedFrom":subQ5}),makeQuery(id+"F3.imprint","IMPRINT",EDGE,{"disambiguationData":[TD([[subQ6,1.0]])],"derivedFrom":subQ5})])]})])],"derivedFrom":subQ3});}
            var Q10;
            {var subQ0=sQuery(id+"F0.wireOp",EDGE,"E0.5");var subQ1=sQuery(id+"F3.wireOp",EDGE,"E11.0");var subQ2=sQuery(id+"F3.wireOp",EDGE,"E2");var subQ3=makeQuery(id+"F3.imprint","INTERSECT",VERTEX,{"derivedFrom":[subQ2,subQ1]});var subQ6=sQuery(id+"F0.wireOp",EDGE,"E0.0");var subQ7=makeQuery(id+"F1.opExtrude","CAP_FACE",FACE,{"disambiguationData":[OSD([subQ6,sQuery(id+"F0.wireOp",EDGE,"E0.1"),sQuery(id+"F0.wireOp",EDGE,"E0.2"),sQuery(id+"F0.wireOp",EDGE,"E0.3"),sQuery(id+"F0.wireOp",EDGE,"E0.4"),subQ0])],"isStart":false});Q10=makeQuery(id+"F4.boolean.opBoolean","SPLIT",FACE,{"disambiguationData":[TD([makeQuery(id+"F4.opExtrude","SWEPT_FACE",FACE,{"disambiguationData":[OSD([subQ2]),TDD([makeQuery(id+"F3.imprint","IMPRINT",EDGE,{"disambiguationData":[TD([[subQ3,-1.0]])],"derivedFrom":subQ2})])]})])],"derivedFrom":subQ7});}
            var Q11;
            {var subQ0=sQuery(id+"F0.wireOp",EDGE,"E0.4");var subQ2=sQuery(id+"F3.wireOp",EDGE,"E3");var subQ4=makeQuery(id+"F1.opExtrude","CAP_FACE",FACE,{"disambiguationData":[OSD([sQuery(id+"F0.wireOp",EDGE,"E0.0"),sQuery(id+"F0.wireOp",EDGE,"E0.1"),sQuery(id+"F0.wireOp",EDGE,"E0.2"),sQuery(id+"F0.wireOp",EDGE,"E0.3"),subQ0,sQuery(id+"F0.wireOp",EDGE,"E0.5")])],"isStart":false});var subQ7=makeQuery(id+"F3.imprint","INTERSECT",VERTEX,{"derivedFrom":[subQ2,sQuery(id+"F3.wireOp",EDGE,"E12.0")]});var subQ8=makeQuery(id+"F3.imprint","INTERSECT",VERTEX,{"derivedFrom":[subQ2,sQuery(id+"F3.wireOp",EDGE,"E8")]});Q11=makeQuery(id+"F4.boolean.opBoolean","SPLIT",FACE,{"disambiguationData":[TD([makeQuery(id+"F4.opExtrude","SWEPT_FACE",FACE,{"disambiguationData":[OSD([subQ2]),TDD([makeQuery(id+"F3.imprint","IMPRINT",EDGE,{"disambiguationData":[TD([[subQ8,1.0]])],"derivedFrom":subQ2}),makeQuery(id+"F3.imprint","IMPRINT",EDGE,{"disambiguationData":[TD([[subQ8,-1.0]])],"derivedFrom":subQ2}),makeQuery(id+"F3.imprint","IMPRINT",EDGE,{"disambiguationData":[TD([[subQ7,-1.0]])],"derivedFrom":subQ2})])]})])],"derivedFrom":subQ4});}
            var Q12;
            {var subQ0=sQuery(id+"F0.wireOp",EDGE,"E0.3");var subQ1=sQuery(id+"F3.wireOp",EDGE,"E3");var subQ2=sQuery(id+"F3.wireOp",EDGE,"E1");var subQ3=makeQuery(id+"F3.imprint","INTERSECT",VERTEX,{"derivedFrom":[subQ2,subQ1]});var subQ4=sQuery(id+"F0.wireOp",EDGE,"E0.4");var subQ5=makeQuery(id+"F1.opExtrude","CAP_FACE",FACE,{"disambiguationData":[OSD([sQuery(id+"F0.wireOp",EDGE,"E0.0"),sQuery(id+"F0.wireOp",EDGE,"E0.1"),sQuery(id+"F0.wireOp",EDGE,"E0.2"),subQ0,subQ4,sQuery(id+"F0.wireOp",EDGE,"E0.5")])],"isStart":false});Q12=makeQuery(id+"F4.boolean.opBoolean","SPLIT",FACE,{"disambiguationData":[TD([makeQuery(id+"F4.opExtrude","SWEPT_FACE",FACE,{"disambiguationData":[OSD([subQ2]),TDD([makeQuery(id+"F3.imprint","IMPRINT",EDGE,{"disambiguationData":[TD([[makeQuery(id+"F3.imprint","INTERSECT",VERTEX,{"derivedFrom":[subQ2,sQuery(id+"F3.wireOp",EDGE,"E19")]}),-1.0]])],"derivedFrom":subQ2}),makeQuery(id+"F3.imprint","IMPRINT",EDGE,{"disambiguationData":[TD([[subQ3,1.0]])],"derivedFrom":subQ2})])]})])],"derivedFrom":subQ5});}
            var Q13;
            {var subQ7=sQuery(id+"F3.wireOp",EDGE,"E6");var subQ8=sQuery(id+"F0.wireOp",EDGE,"E0.2");var subQ9=makeQuery(id+"F1.opExtrude","CAP_FACE",FACE,{"disambiguationData":[OSD([sQuery(id+"F0.wireOp",EDGE,"E0.0"),sQuery(id+"F0.wireOp",EDGE,"E0.1"),subQ8,sQuery(id+"F0.wireOp",EDGE,"E0.3"),sQuery(id+"F0.wireOp",EDGE,"E0.4"),sQuery(id+"F0.wireOp",EDGE,"E0.5")])],"isStart":false});Q13=makeQuery(id+"F4.boolean.opBoolean","SPLIT",FACE,{"disambiguationData":[TD([makeQuery(id+"F4.opExtrude","SWEPT_FACE",FACE,{"disambiguationData":[OSD([subQ7])]})])],"derivedFrom":subQ9});}
            chamfer(context, id + "F5", {"entities" : qUnion([Q0, Q1, Q2, Q3, Q4, Q5, Q6, Q7, Q8, Q9, Q10, Q11, Q12, Q13]), "width" : 0.13 * mm});
        }
    });
